# Revit family: Rotary_Mail_Center-Salsbury_Industries-Free_Standing-Brass_Americana_Style
name_source: partatom
category: Specialty Equipment
revit_build: Autodesk Revit 2016 (Build: 20150714_1515(x64)
units: mm (PartAtom-declared; Revit-internal decimal feet)

## family parameters
Always vertical = Yes
Cut with Voids When Loaded = No
OmniClass Number = 23.40.90.14.11
OmniClass Title = Mail Boxes
Part Type = Normal
Room Calculation Point = No
Round Connector Dimension = Use Diameter
Shared = No
Work Plane-Based = No

## types (1)
- 3150
    2016RL - Door Material = Brass Die Cast - Salsbury Finish - Brass
    2016RL - Door Material - Textured = Brass Die Cast - Salsbury Finish - Textured
    2016RL - Door Window Material = Glass - Salsbury Finish - Clear
    2016RL - Enclosure Material = Steel - Salsbury Finish - Tan
    2016RL - Lock Material = Stainless Steel - Salsbury Finish - Gold
    2016RL - Name Plate Material = Aluminum - Salsbury Finish -  Brushed Steel
    Assembly Code = C1030910
    Assembly Description = Mailboxes
    Compatibility = Mail Center works with Brass and Americana Mailboxes (order mailboxes separately)
    Depth = 24 "
    Description = Brass/Americana Style - Private Access (Includes Master Commercial Lock)
    Height = 73.625 "
    Interior Material = Steel - Salsbury Finish - Clear
    Lock Material = Stainless Steel - Salsbury Finish -  Polished
    Manufacturer = Salsbury Industries
    MasterFormat Number = 10 55 00
    MasterFormat Title = Postal Specialties
    Model = 3150
    OmniClass 23 Number = 23.40.90.14.11
    OmniClass 23 Title = Mail Boxes
    Rotating Frame Body Finish = Steel - Salsbury Finish - Clear
    Rotating Frame Trim Finish = Steel - Salsbury Finish - Black
    Type Comments = Rotary Mail Center (Order Mailboxes Separately)
    URL = www.mailboxes.com
    Version = 1.0 (05/31/19)
    Width = 30 "

## geometry (parser evidence)
native form markers: Blend x2, Sweep x12
no freeform markers — native parametric forms only
